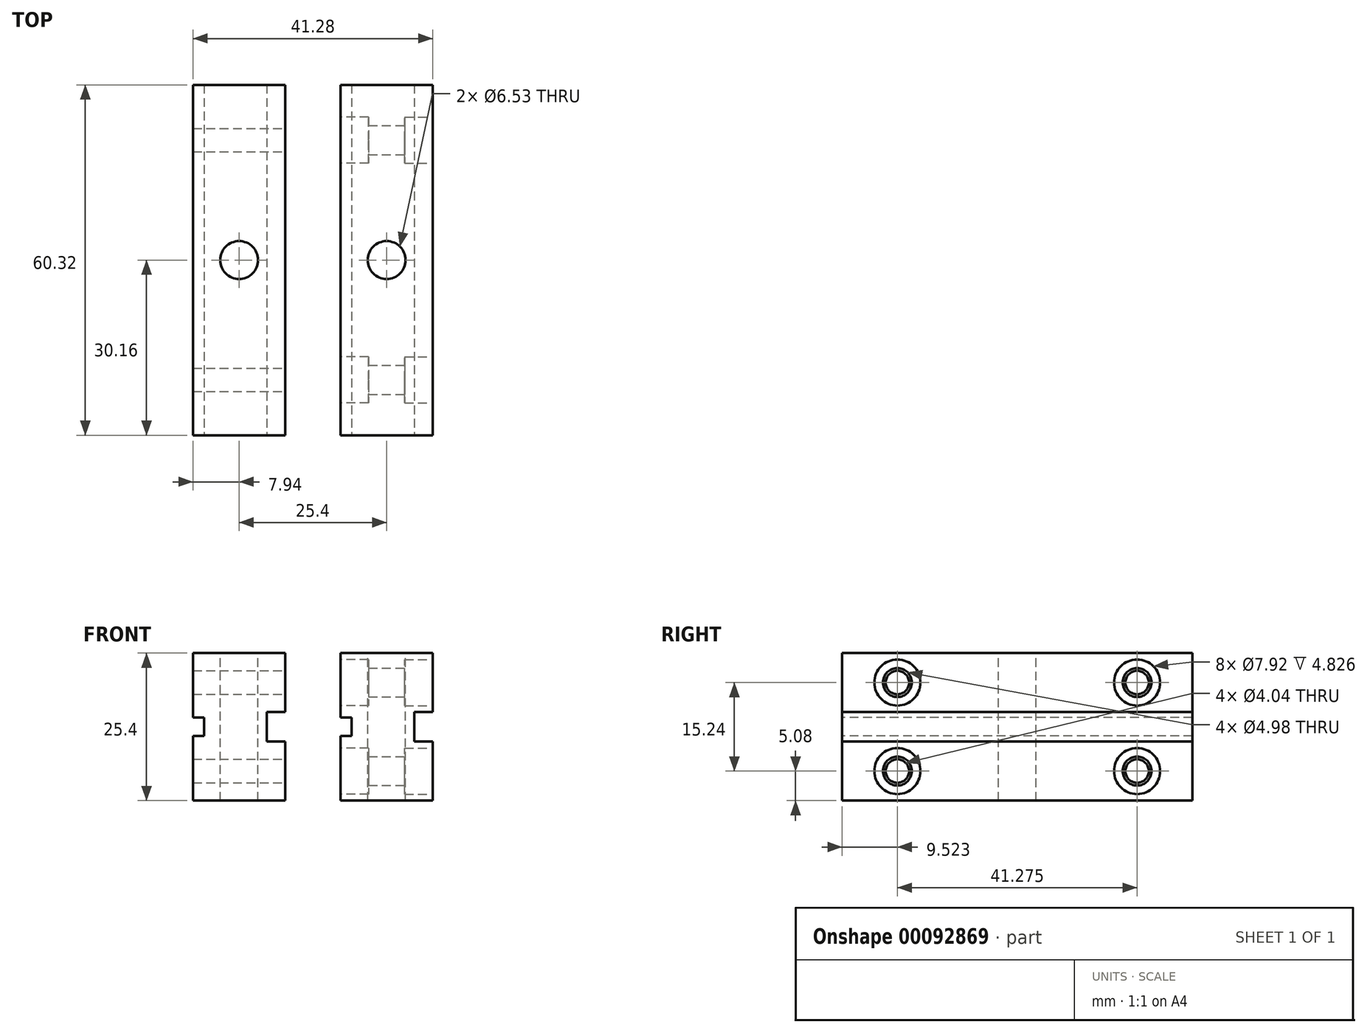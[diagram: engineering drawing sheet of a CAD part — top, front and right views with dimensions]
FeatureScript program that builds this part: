
annotation { "Feature Type Name" : "Feature", "Feature Type Description" : "" }
export const myFeature = defineFeature(function(context is Context, id is Id, definition is map)
    precondition{}
    {
        {
            var Q0;
            Q0=qCreatedBy(makeId("Top.planeOp"),FACE);
            var sketch = newSketch(context, id + "F0", { "sketchPlane" : qUnion([Q0])});
            skLineSegment(sketch, "E0.bottom", {"start": v(7.94, 30.16) * mm, "end": v(-7.94, 30.16) * mm});
            skLineSegment(sketch, "E0.top", {"start": v(7.94, -30.16) * mm, "end": v(-7.94, -30.16) * mm});
            skLineSegment(sketch, "E0.left", {"start": v(7.94, 30.16) * mm, "end": v(7.94, -30.16) * mm});
            skLineSegment(sketch, "E0.right", {"start": v(-7.94, 30.16) * mm, "end": v(-7.94, -30.16) * mm});
            skPoint(sketch, "E0.middle", {"position": v(0, 0) * mm});
            skSolve(sketch);
        }
        {
            var Q0;
            Q0=makeQuery(id+"F0.imprint","IMPRINT",FACE,{"disambiguationData":[TD([[makeQuery(id+"F0.imprint","IMPRINT",EDGE,{"derivedFrom":sQuery(id+"F0.wireOp",EDGE,"E0.bottom")}),1.0]])]});
            extrude(context, id + "F1", {"entities" : qUnion([Q0]), "depth" : 25.4 * mm});
        }
        {
            var Q0;
            Q0=makeQuery(id+"F1.opExtrude","CAP_FACE",FACE,{"disambiguationData":[OSD([sQuery(id+"F0.wireOp",EDGE,"E0.bottom"),sQuery(id+"F0.wireOp",EDGE,"E0.top"),sQuery(id+"F0.wireOp",EDGE,"E0.left"),sQuery(id+"F0.wireOp",EDGE,"E0.right")])],"isStart":false});
            var sketch = newSketch(context, id + "F2", { "sketchPlane" : qUnion([Q0])});
            skLineSegment(sketch, "E1.0.0", {"start": v(7.94, -30.16) * mm, "end": v(7.94, 30.16) * mm, "construction": true});
            skLineSegment(sketch, "E1.0.1", {"start": v(7.94, 30.16) * mm, "end": v(-7.94, 30.16) * mm, "construction": true});
            skLineSegment(sketch, "E1.0.2", {"start": v(-7.94, 30.16) * mm, "end": v(-7.94, -30.16) * mm, "construction": true});
            skLineSegment(sketch, "E1.0.3", {"start": v(-7.94, -30.16) * mm, "end": v(7.94, -30.16) * mm, "construction": true});
            skLineSegment(sketch, "E2", {"start": v(0, 30.16) * mm, "end": v(0, -30.16) * mm, "construction": true});
            skPoint(sketch, "E3", {"position": v(0, 0) * mm});
            skSolve(sketch);
        }
        {
            var Q0;
            Q0=sQuery(id+"F2.wireOp",VERTEX,"E3");
            var Q1;
            Q1=makeQuery(id+"F1.opExtrude","SWEPT_BODY",BODY,{"disambiguationData":[OSD([sQuery(id+"F0.wireOp",EDGE,"E0.bottom"),sQuery(id+"F0.wireOp",EDGE,"E0.top"),sQuery(id+"F0.wireOp",EDGE,"E0.left"),sQuery(id+"F0.wireOp",EDGE,"E0.right")])]});
            hole(context, id + "F3", {"style" : HoleStyle.SIMPLE, "endStyle" : HoleEndStyle.THROUGH, "standardTappedOrClearance" : lookupTablePath({ "standard" : "ANSI", "fit" : "Close", "size" : "1/4", "type" : "Clearance" }), "standardBlindInLast" : lookupTablePath({ "fit" : "Close", "standard" : "ANSI", "size" : "1/4", "type" : "Clearance" }), "holeDiameter" : 6.53 * mm, "locations" : qUnion([Q0]), "scope" : qUnion([Q1]), "isTappedThrough" : true});
        }
        {
            var Q0;
            Q0=makeQuery(id+"F1.opExtrude","SWEPT_FACE",FACE,{"disambiguationData":[OSD([sQuery(id+"F0.wireOp",EDGE,"E0.left")])]});
            var sketch = newSketch(context, id + "F4", { "sketchPlane" : qUnion([Q0])});
            skLineSegment(sketch, "E4.0.0", {"start": v(-30.16, 0) * mm, "end": v(30.16, 0) * mm});
            skLineSegment(sketch, "E4.0.1", {"start": v(30.16, 0) * mm, "end": v(30.16, 25.4) * mm});
            skLineSegment(sketch, "E4.0.2", {"start": v(30.16, 25.4) * mm, "end": v(-30.16, 25.4) * mm});
            skLineSegment(sketch, "E4.0.3", {"start": v(-30.16, 25.4) * mm, "end": v(-30.16, 0) * mm});
            skLineSegment(sketch, "E5", {"start": v(30.16, 20.32) * mm, "end": v(-30.16, 20.32) * mm, "construction": true});
            skLineSegment(sketch, "E6", {"start": v(30.16, 5.08) * mm, "end": v(-30.16, 5.08) * mm, "construction": true});
            skLineSegment(sketch, "E7", {"start": v(0, 25.4) * mm, "end": v(0, 0) * mm, "construction": true});
            skLineSegment(sketch, "E8", {"start": v(20.64, 25.4) * mm, "end": v(20.64, 0) * mm, "construction": true});
            skLineSegment(sketch, "E9", {"start": v(-20.64, 25.4) * mm, "end": v(-20.64, 0) * mm, "construction": true});
            skLineSegment(sketch, "E10", {"start": v(30.16, 15.24) * mm, "end": v(-30.16, 15.24) * mm, "construction": true});
            skLineSegment(sketch, "E11", {"start": v(30.16, 10.16) * mm, "end": v(-30.16, 10.16) * mm, "construction": true});
            skPoint(sketch, "E12", {"position": v(30.16, 12.7) * mm});
            skPoint(sketch, "E13", {"position": v(20.64, 20.32) * mm});
            skPoint(sketch, "E14", {"position": v(20.64, 5.08) * mm});
            skPoint(sketch, "E15", {"position": v(-20.64, 5.08) * mm});
            skPoint(sketch, "E16", {"position": v(-20.64, 20.32) * mm});
            skLineSegment(sketch, "E17", {"start": v(30.16, 15.24) * mm, "end": v(-30.16, 15.24) * mm});
            skLineSegment(sketch, "E18", {"start": v(30.16, 10.16) * mm, "end": v(-30.16, 10.16) * mm});
            skSolve(sketch);
        }
        {
            var Q0;
            {var subQ0=sQuery(id+"F4.wireOp",EDGE,"E17");Q0=makeQuery(id+"F4.imprint","IMPRINT",FACE,{"disambiguationData":[TD([[makeQuery(id+"F4.imprint","IMPRINT",EDGE,{"derivedFrom":subQ0}),1.0]])]});}
            extrude(context, id + "F5", {"entities" : qUnion([Q0]), "operationType" : NewBodyOperationType.REMOVE, "oppositeDirection" : true, "depth" : 3.17 * mm});
        }
        {
            var Q0;
            Q0=makeQuery(id+"F1.opExtrude","SWEPT_FACE",FACE,{"disambiguationData":[OSD([sQuery(id+"F0.wireOp",EDGE,"E0.right")])]});
            var sketch = newSketch(context, id + "F6", { "sketchPlane" : qUnion([Q0])});
            skPoint(sketch, "E19.0", {"position": v(-30.16, 12.7) * mm});
            skLineSegment(sketch, "E20", {"start": v(-30.16, 11.11) * mm, "end": v(30.16, 11.11) * mm, "construction": true});
            skLineSegment(sketch, "E21", {"start": v(-30.16, 14.29) * mm, "end": v(30.16, 14.29) * mm, "construction": true});
            skLineSegment(sketch, "E22", {"start": v(-30.16, 11.11) * mm, "end": v(30.16, 11.11) * mm});
            skLineSegment(sketch, "E23", {"start": v(-30.16, 14.29) * mm, "end": v(30.16, 14.29) * mm});
            skSolve(sketch);
        }
        {
            var Q0;
            {var subQ0=sQuery(id+"F6.wireOp",EDGE,"E22");Q0=makeQuery(id+"F6.imprint","IMPRINT",FACE,{"disambiguationData":[TD([[makeQuery(id+"F6.imprint","IMPRINT",EDGE,{"derivedFrom":subQ0}),1.0]])]});}
            extrude(context, id + "F7", {"entities" : qUnion([Q0]), "operationType" : NewBodyOperationType.REMOVE, "oppositeDirection" : true, "depth" : 1.9 * mm});
        }
        {
            var Q0;
            Q0=makeQuery(id+"F1.opExtrude","SWEPT_BODY",BODY,{"disambiguationData":[OSD([sQuery(id+"F0.wireOp",EDGE,"E0.bottom"),sQuery(id+"F0.wireOp",EDGE,"E0.top"),sQuery(id+"F0.wireOp",EDGE,"E0.left"),sQuery(id+"F0.wireOp",EDGE,"E0.right")])]});
            var Q1;
            {var subQ0=sQuery(id+"F4.wireOp",EDGE,"E4.0.2");Q1=makeQuery(id+"F4.imprint","IMPRINT",FACE,{"disambiguationData":[TD([[makeQuery(id+"F4.imprint","IMPRINT",EDGE,{"derivedFrom":subQ0}),1.0]])]});}
            transform(context, id + "F8", {"entities" : qUnion([Q0]), "transformType" : TransformType.TRANSLATION_DISTANCE, "transformDirection" : qUnion([Q1]), "distance" : 25.4 * mm, "makeCopy" : true});
        }
        {
            var Q0;
            {var subQ0=sQuery(id+"F4.wireOp",EDGE,"E4.0.2");Q0=makeQuery(id+"F4.imprint","IMPRINT",FACE,{"disambiguationData":[TD([[makeQuery(id+"F4.imprint","IMPRINT",EDGE,{"derivedFrom":subQ0}),1.0]])]});}
            var sketch = newSketch(context, id + "F9", { "sketchPlane" : qUnion([Q0])});
            skPoint(sketch, "E24.0", {"position": v(-20.64, 20.32) * mm});
            skPoint(sketch, "E25.0", {"position": v(20.64, 20.32) * mm});
            skPoint(sketch, "E26.0", {"position": v(20.64, 5.08) * mm});
            skPoint(sketch, "E27.0", {"position": v(-20.64, 5.08) * mm});
            skSolve(sketch);
        }
        {
            var Q0;
            Q0=sQuery(id+"F9.wireOp",VERTEX,"E24.0");
            var Q1;
            Q1=sQuery(id+"F9.wireOp",VERTEX,"E27.0");
            var Q2;
            Q2=sQuery(id+"F9.wireOp",VERTEX,"E26.0");
            var Q3;
            Q3=sQuery(id+"F9.wireOp",VERTEX,"E25.0");
            var Q4;
            Q4=makeQuery(id+"F1.opExtrude","SWEPT_BODY",BODY,{"disambiguationData":[OSD([sQuery(id+"F0.wireOp",EDGE,"E0.bottom"),sQuery(id+"F0.wireOp",EDGE,"E0.top"),sQuery(id+"F0.wireOp",EDGE,"E0.left"),sQuery(id+"F0.wireOp",EDGE,"E0.right")])]});
            hole(context, id + "F10", {"style" : HoleStyle.SIMPLE, "endStyle" : HoleEndStyle.THROUGH, "standardTappedOrClearance" : lookupTablePath({ "standard" : "ANSI", "engagement" : "75%", "pitch" : "32 tpi", "size" : "#10", "type" : "Tapped" }), "standardBlindInLast" : lookupTablePath({ "standard" : "ANSI", "engagement" : "75%", "pitch" : "32 tpi", "size" : "#10", "type" : "Tapped" }), "holeDiameter" : 4.04 * mm, "locations" : qUnion([Q0, Q1, Q2, Q3]), "scope" : qUnion([Q4]), "isTappedThrough" : true, "majorDiameter" : 4.83 * mm, "showTappedDepth" : true});
        }
        {
            var Q0;
            {var subQ1=sQuery(id+"F0.wireOp",EDGE,"E0.left");Q0=makeQuery(id+"F8.opPattern","COPY",FACE,{"derivedFrom":makeQuery(id+"F5.boolean.opBoolean","SPLIT",FACE,{"disambiguationData":[TD([makeQuery(id+"F5.opExtrude","SWEPT_FACE",FACE,{"disambiguationData":[OSD([sQuery(id+"F4.wireOp",EDGE,"E17")])]})])],"derivedFrom":makeQuery(id+"F1.opExtrude","SWEPT_FACE",FACE,{"disambiguationData":[OSD([subQ1])]})}),"instanceName":"1"});}
            var sketch = newSketch(context, id + "F11", { "sketchPlane" : qUnion([Q0])});
            skPoint(sketch, "E28.0", {"position": v(-20.64, 20.32) * mm});
            skPoint(sketch, "E29.0", {"position": v(20.64, 20.32) * mm});
            skPoint(sketch, "E30.0", {"position": v(20.64, 5.08) * mm});
            skPoint(sketch, "E31.0", {"position": v(-20.64, 5.08) * mm});
            skSolve(sketch);
        }
        {
            var Q0;
            Q0=sQuery(id+"F11.wireOp",VERTEX,"E28.0");
            var Q1;
            Q1=sQuery(id+"F11.wireOp",VERTEX,"E29.0");
            var Q2;
            Q2=sQuery(id+"F11.wireOp",VERTEX,"E30.0");
            var Q3;
            Q3=sQuery(id+"F11.wireOp",VERTEX,"E31.0");
            var Q4;
            Q4=makeQuery(id+"F8.opPattern","COPY",BODY,{"derivedFrom":makeQuery(id+"F1.opExtrude","SWEPT_BODY",BODY,{"disambiguationData":[OSD([sQuery(id+"F0.wireOp",EDGE,"E0.bottom"),sQuery(id+"F0.wireOp",EDGE,"E0.top"),sQuery(id+"F0.wireOp",EDGE,"E0.left"),sQuery(id+"F0.wireOp",EDGE,"E0.right")])]}),"instanceName":"1"});
            hole(context, id + "F12", {"style" : HoleStyle.C_BORE, "endStyle" : HoleEndStyle.THROUGH, "holeDiameter" : 4.98 * mm, "cBoreDiameter" : 7.92 * mm, "cBoreDepth" : 4.83 * mm, "locations" : qUnion([Q0, Q1, Q2, Q3]), "scope" : qUnion([Q4]), "isTappedThrough" : true});
        }
        {
            var Q0;
            {var subQ0=sQuery(id+"F4.wireOp",EDGE,"E4.0.2");Q0=makeQuery(id+"F4.imprint","IMPRINT",FACE,{"disambiguationData":[TD([[makeQuery(id+"F4.imprint","IMPRINT",EDGE,{"derivedFrom":subQ0}),1.0]])]});}
            var sketch = newSketch(context, id + "F13", { "sketchPlane" : qUnion([Q0])});
            skPoint(sketch, "E32.0", {"position": v(20.64, 20.32) * mm});
            skPoint(sketch, "E33.0", {"position": v(20.64, 5.08) * mm});
            skPoint(sketch, "E34.0", {"position": v(-20.64, 5.08) * mm});
            skPoint(sketch, "E35.0", {"position": v(-20.64, 20.32) * mm});
            skSolve(sketch);
        }
        {
            var Q0;
            Q0=sQuery(id+"F13.wireOp",VERTEX,"E32.0");
            var Q1;
            Q1=sQuery(id+"F13.wireOp",VERTEX,"E35.0");
            var Q2;
            Q2=sQuery(id+"F13.wireOp",VERTEX,"E34.0");
            var Q3;
            Q3=sQuery(id+"F13.wireOp",VERTEX,"E33.0");
            var Q4;
            Q4=makeQuery(id+"F8.opPattern","COPY",BODY,{"derivedFrom":makeQuery(id+"F1.opExtrude","SWEPT_BODY",BODY,{"disambiguationData":[OSD([sQuery(id+"F0.wireOp",EDGE,"E0.bottom"),sQuery(id+"F0.wireOp",EDGE,"E0.top"),sQuery(id+"F0.wireOp",EDGE,"E0.left"),sQuery(id+"F0.wireOp",EDGE,"E0.right")])]}),"instanceName":"1"});
            hole(context, id + "F14", {"style" : HoleStyle.C_BORE, "endStyle" : HoleEndStyle.THROUGH, "oppositeDirection" : true, "holeDiameter" : 4.98 * mm, "cBoreDiameter" : 7.92 * mm, "cBoreDepth" : 4.83 * mm, "locations" : qUnion([Q0, Q1, Q2, Q3]), "scope" : qUnion([Q4]), "isTappedThrough" : true});
        }
    });
